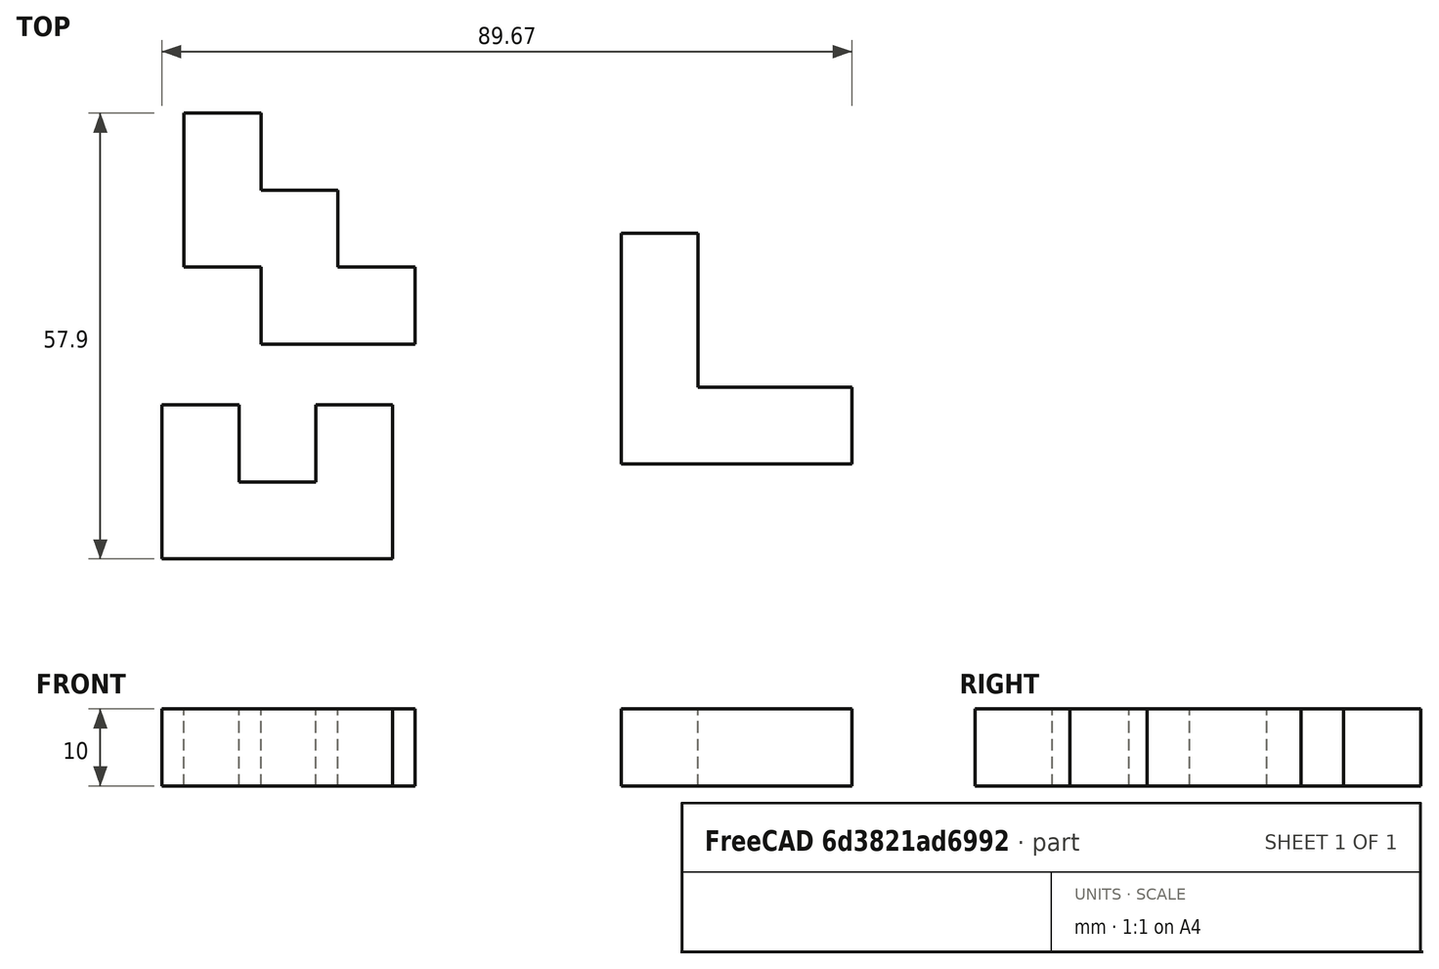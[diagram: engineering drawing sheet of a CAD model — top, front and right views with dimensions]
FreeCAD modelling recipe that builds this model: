
FCSTD DOCUMENT  (FreeCAD 0.16R)
Label: UVandW
License: All rights reserved
LicenseURL: http://en.wikipedia.org/wiki/All_rights_reserved
objects: Sketcher::SketchObject×3, PartDesign::Pad×3, Mesh::Feature×3
note: 9 computed .brp shape members not serialized (recipe doc carries the construction recipe); baked Part::Feature solids carry a one-line shape summary decoded from their .brp

FEATURE [Sketcher::SketchObject] Sketch003
  sketch-geometry (8):
    g0: LineSegment StartX=-30 StartY=20 StartZ=0 EndX=-30 EndY=0 EndZ=0
    g1: LineSegment StartX=-30 StartY=0 StartZ=0 EndX=0 EndY=0 EndZ=0
    g2: LineSegment StartX=0 StartY=0 StartZ=0 EndX=0 EndY=20 EndZ=0
    g3: LineSegment StartX=0 StartY=20 StartZ=0 EndX=-10 EndY=20 EndZ=0
    g4: LineSegment StartX=-10 StartY=10 StartZ=0 EndX=-20 EndY=10 EndZ=0
    g5: LineSegment StartX=-20 StartY=10 StartZ=0 EndX=-20 EndY=20 EndZ=0
    g6: LineSegment StartX=-20 StartY=20 StartZ=0 EndX=-30 EndY=20 EndZ=0
    g7: LineSegment StartX=-10 StartY=10 StartZ=0 EndX=-10 EndY=20 EndZ=0
  constraints (23):
    c: Vertical(g0)
    c: Coincident(g0,g1)
    c: Horizontal(g1)
    c: Coincident(g1,g2)
    c: Vertical(g2)
    c: Coincident(g2,g3)
    c: Coincident(g4,g5)
    c: Coincident(g5,g6)
    c: Coincident(g6,g0)
    c: Distance(g2) = 20
    c: Distance(g3) = 10
    c: Distance(g4) = 10
    c: Distance(g5) = 10
    c: Distance(g0) = 20
    c: Perpendicular(g2,g3)
    c: Coincident(g7,g4)
    c: Coincident(g7,g3)
    c: Vertical(g7)
    c: Perpendicular(g5,g4)
    c: Perpendicular(g6,g0)
    c: Horizontal(g4)
    c: Distance(g6) = 10
    c: Coincident(g1,g-1)
FEATURE [PartDesign::Pad] Pad
  Length = 10
  Length2 = 100
  Sketch = -> Sketch003
  Type = 0
FEATURE [Sketcher::SketchObject] Sketch
  sketch-geometry (6):
    g0: LineSegment StartX=29.6683 StartY=42.3125 StartZ=0 EndX=29.6683 EndY=12.3125 EndZ=0
    g1: LineSegment StartX=29.6683 StartY=12.3125 StartZ=0 EndX=59.6683 EndY=12.3125 EndZ=0
    g2: LineSegment StartX=59.6683 StartY=12.3125 StartZ=0 EndX=59.6683 EndY=22.3125 EndZ=0
    g3: LineSegment StartX=59.6683 StartY=22.3125 StartZ=0 EndX=39.6683 EndY=22.3125 EndZ=0
    g4: LineSegment StartX=39.6683 StartY=22.3125 StartZ=0 EndX=39.6683 EndY=42.3125 EndZ=0
    g5: LineSegment StartX=39.6683 StartY=42.3125 StartZ=0 EndX=29.6683 EndY=42.3125 EndZ=0
  constraints (16):
    c: Coincident(g0,g1)
    c: Horizontal(g1)
    c: Coincident(g1,g2)
    c: Coincident(g2,g3)
    c: Horizontal(g3)
    c: Coincident(g3,g4)
    c: Vertical(g4)
    c: Coincident(g4,g5)
    c: Coincident(g5,g0)
    c: Distance(g0) = 30
    c: Distance(g4) = 20
    c: Distance(g3) = 20
    c: Distance(g5) = 10
    c: Distance(g1) = 30
    c: Perpendicular(g1,g2)
    c: Perpendicular(g5,g0)
FEATURE [PartDesign::Pad] Pad001
  Length = 10
  Length2 = 100
  Sketch = -> Sketch
  Type = 0
FEATURE [Sketcher::SketchObject] Sketch004
  sketch-geometry (10):
    g0: LineSegment StartX=-27.1226 StartY=57.8996 StartZ=0 EndX=-27.1226 EndY=37.8996 EndZ=0
    g1: LineSegment StartX=-27.1226 StartY=37.8996 StartZ=0 EndX=-17.1226 EndY=37.8996 EndZ=0
    g2: LineSegment StartX=-17.1226 StartY=37.8996 StartZ=0 EndX=-17.1226 EndY=27.8996 EndZ=0
    g3: LineSegment StartX=-17.1226 StartY=27.8996 StartZ=0 EndX=2.87745 EndY=27.8996 EndZ=0
    g4: LineSegment StartX=2.87745 StartY=27.8996 StartZ=0 EndX=2.87745 EndY=37.8996 EndZ=0
    g5: LineSegment StartX=2.87745 StartY=37.8996 StartZ=0 EndX=-7.12255 EndY=37.8996 EndZ=0
    g6: LineSegment StartX=-7.12255 StartY=37.8996 StartZ=0 EndX=-7.12255 EndY=47.8996 EndZ=0
    g7: LineSegment StartX=-7.12255 StartY=47.8996 StartZ=0 EndX=-17.1226 EndY=47.8996 EndZ=0
    g8: LineSegment StartX=-17.1226 StartY=47.8996 StartZ=0 EndX=-17.1226 EndY=57.8996 EndZ=0
    g9: LineSegment StartX=-17.1226 StartY=57.8996 StartZ=0 EndX=-27.1226 EndY=57.8996 EndZ=0
  constraints (30):
    c: Coincident(g0,g1)
    c: Coincident(g1,g2)
    c: Coincident(g2,g3)
    c: Coincident(g3,g4)
    c: Vertical(g4)
    c: Coincident(g4,g5)
    c: Coincident(g5,g6)
    c: Coincident(g6,g7)
    c: Coincident(g7,g8)
    c: Coincident(g8,g9)
    c: Coincident(g9,g0)
    c: Distance(g0) = 20
    c: Distance(g1) = 10
    c: Distance(g2) = 10
    c: Distance(g9) = 10
    c: Distance(g8) = 10
    c: Distance(g7) = 10
    c: Distance(g3) = 20
    c: Distance(g4) = 10
    c: Distance(g5) = 10
    c: Distance(g6) = 10
    c: Perpendicular(g8,g9)
    c: Perpendicular(g9,g0)
    c: Perpendicular(g1,g0)
    c: Perpendicular(g2,g1)
    c: Perpendicular(g3,g4)
    c: Perpendicular(g6,g7)
    c: Perpendicular(g6,g5)
    c: DistanceX(g6) = -7.12255
    c: DistanceY(g6) = 47.8996
FEATURE [PartDesign::Pad] Pad002
  Length = 10
  Length2 = 100
  Sketch = -> Sketch004
  Type = 0
FEATURE [Mesh::Feature] Mesh  label="Pad (Meshed)"
FEATURE [Mesh::Feature] Mesh001  label="Pad (Meshed)001"
FEATURE [Mesh::Feature] Mesh002  label="Pad001 (Meshed)"
